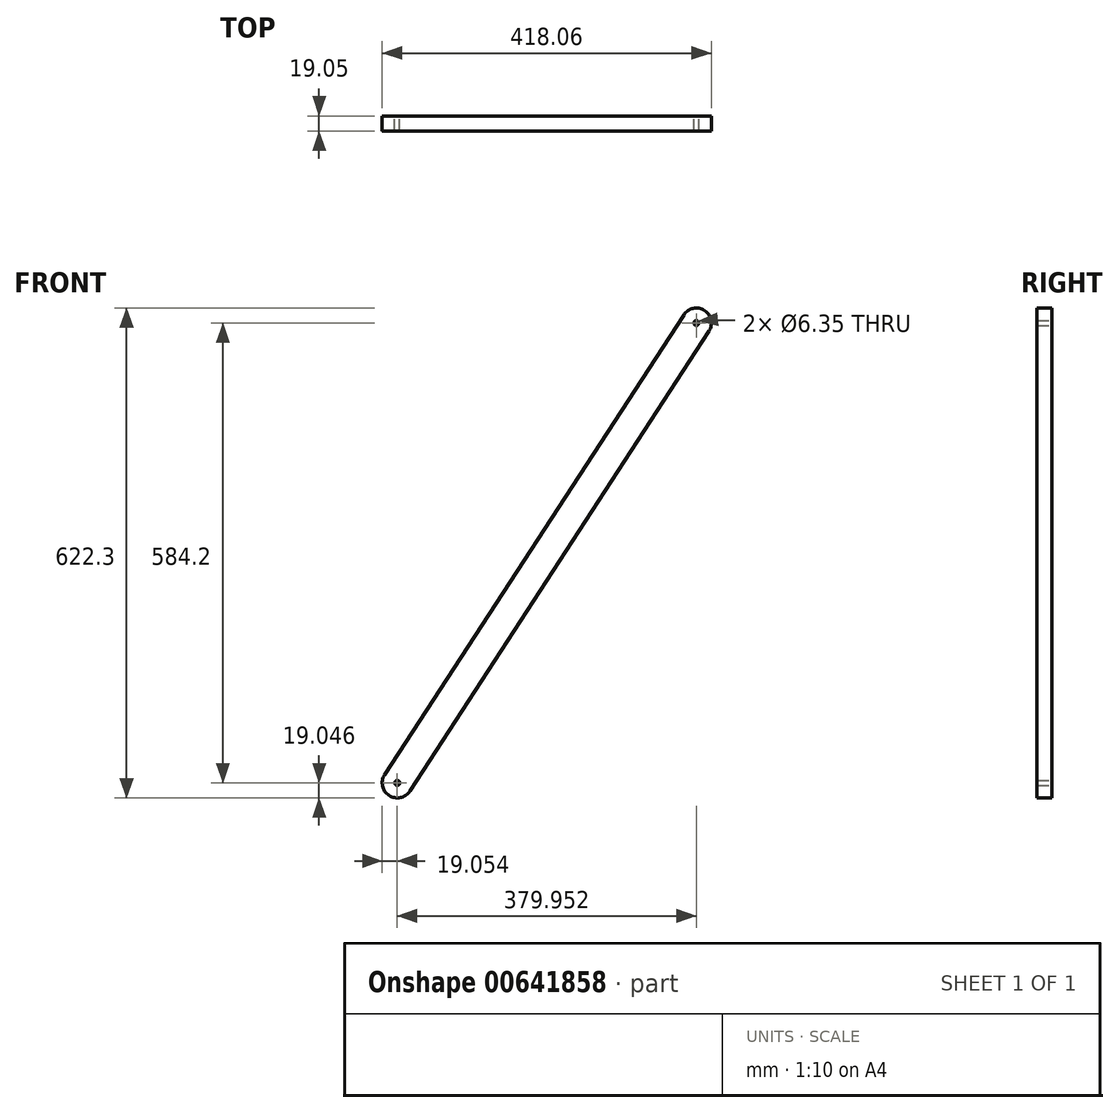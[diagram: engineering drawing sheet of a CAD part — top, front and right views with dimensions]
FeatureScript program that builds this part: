
annotation { "Feature Type Name" : "Feature", "Feature Type Description" : "" }
export const myFeature = defineFeature(function(context is Context, id is Id, definition is map)
    precondition{}
    {
        {
            var Q0;
            Q0=qCreatedBy(makeId("Front.planeOp"),FACE);
            var sketch = newSketch(context, id + "F0", { "sketchPlane" : qUnion([Q0])});
            skLineSegment(sketch, "E0.bottom", {"start": v(-219.88, -432.71) * mm, "end": v(288.12, -432.71) * mm});
            skLineSegment(sketch, "E0.top", {"start": v(-219.88, 583.29) * mm, "end": v(288.12, 583.29) * mm, "construction": true});
            skLineSegment(sketch, "E0.left", {"start": v(-219.88, -432.71) * mm, "end": v(-219.88, 583.29) * mm, "construction": true});
            skLineSegment(sketch, "E0.right", {"start": v(288.12, -432.71) * mm, "end": v(288.12, 583.29) * mm, "construction": true});
            skLineSegment(sketch, "E1", {"start": v(-219.88, 278.49) * mm, "end": v(288.12, 278.49) * mm, "construction": true});
            skLineSegment(sketch, "E2", {"start": v(-219.88, -77.11) * mm, "end": v(288.12, -77.11) * mm, "construction": true});
            skLineSegment(sketch, "E3", {"start": v(-219.88, -432.71) * mm, "end": v(160.08, 151.49) * mm, "construction": true});
            skLineSegment(sketch, "E4", {"start": v(160.08, 151.49) * mm, "end": v(-219.88, 278.49) * mm, "construction": true});
            skLineSegment(sketch, "E5", {"start": v(288.12, -432.71) * mm, "end": v(-91.83, -305.71) * mm, "construction": true});
            skLineSegment(sketch, "E6", {"start": v(-91.83, -305.71) * mm, "end": v(288.12, 278.49) * mm, "construction": true});
            skArc(sketch, "E7", {"start": v(-599.83, 151.49) * mm, "mid": v(-219.88, -122.13) * mm, "end": v(160.08, 151.49) * mm, "construction": true});
            skArc(sketch, "E8", {"start": v(160.08, 151.49) * mm, "mid": v(-219.88, 264.17) * mm, "end": v(-599.83, 151.49) * mm, "construction": true});
            skArc(sketch, "E9", {"start": v(-418.38, 235.3) * mm, "mid": v(-219.88, 182.66) * mm, "end": v(-21.37, 235.3) * mm, "construction": true});
            skLineSegment(sketch, "E10", {"start": v(-418.38, 235.3) * mm, "end": v(-219.88, 583.29) * mm, "construction": true});
            skLineSegment(sketch, "E11", {"start": v(-219.88, -432.71) * mm, "end": v(-418.38, 235.3) * mm, "construction": true});
            skArc(sketch, "E12", {"start": v(668.08, -305.7) * mm, "mid": v(288.12, -32.1) * mm, "end": v(-91.83, -305.7) * mm, "construction": true});
            skArc(sketch, "E13", {"start": v(-91.83, -305.7) * mm, "mid": v(288.12, -418.4) * mm, "end": v(668.08, -305.7) * mm, "construction": true});
            skArc(sketch, "E14.trimOffspring", {"start": v(89.62, -84.73) * mm, "mid": v(288.12, -113.6) * mm, "end": v(486.63, -84.73) * mm, "construction": true});
            skLineSegment(sketch, "E15", {"start": v(288.12, -432.71) * mm, "end": v(486.63, -84.73) * mm, "construction": true});
            skLineSegment(sketch, "E16", {"start": v(486.63, -84.73) * mm, "end": v(288.12, 583.29) * mm, "construction": true});
            skArc(sketch, "E17", {"start": v(-213.84, 296.55) * mm, "mid": v(-237.94, 284.52) * mm, "end": v(-225.91, 260.42) * mm, "construction": true});
            skArc(sketch, "E18", {"start": v(-235.85, -422.33) * mm, "mid": v(-230.26, -448.68) * mm, "end": v(-203.9, -443.1) * mm});
            skLineSegment(sketch, "E19", {"start": v(144.1, 161.87) * mm, "end": v(-235.85, -422.33) * mm});
            skLineSegment(sketch, "E20", {"start": v(-219.88, -432.71) * mm, "end": v(-235.85, -422.33) * mm, "construction": true});
            skLineSegment(sketch, "E21", {"start": v(176.05, 141.1) * mm, "end": v(-203.9, -443.1) * mm});
            skLineSegment(sketch, "E22", {"start": v(-219.88, -432.71) * mm, "end": v(-203.9, -443.1) * mm, "construction": true});
            skArc(sketch, "E23.trimOffspring", {"start": v(176.05, 141.1) * mm, "mid": v(170.35, 167.53) * mm, "end": v(143.97, 161.65) * mm});
            skCircle(sketch, "E24", {"center": v(160.08, 151.49) * mm, "radius": 3.18 * mm});
            skLineSegment(sketch, "E25.0", {"start": v(166.12, 169.55) * mm, "end": v(-213.84, 296.55) * mm, "construction": true});
            skLineSegment(sketch, "E26.trimOffspring", {"start": v(130.68, 141.23) * mm, "end": v(-225.91, 260.42) * mm, "construction": true});
            skCircle(sketch, "E27", {"center": v(160.08, 151.49) * mm, "radius": 19.05 * mm, "construction": true});
            skLineSegment(sketch, "E28", {"start": v(130.68, 141.23) * mm, "end": v(154.04, 133.42) * mm, "construction": true});
            skLineSegment(sketch, "E29", {"start": v(154.04, 133.42) * mm, "end": v(160.08, 151.49) * mm, "construction": true});
            skCircle(sketch, "E30", {"center": v(-219.88, -432.71) * mm, "radius": 3.18 * mm});
            skCircle(sketch, "E31", {"center": v(-219.88, 278.49) * mm, "radius": 3.18 * mm, "construction": true});
            skSolve(sketch);
        }
        {
            var Q0;
            Q0 = qSketchRegion(id + "F0", true);
            extrude(context, id + "F1", {"entities" : qUnion([Q0]), "depth" : 19.05 * mm, "offsetDistance" : 25.4 * mm});
        }
    });
